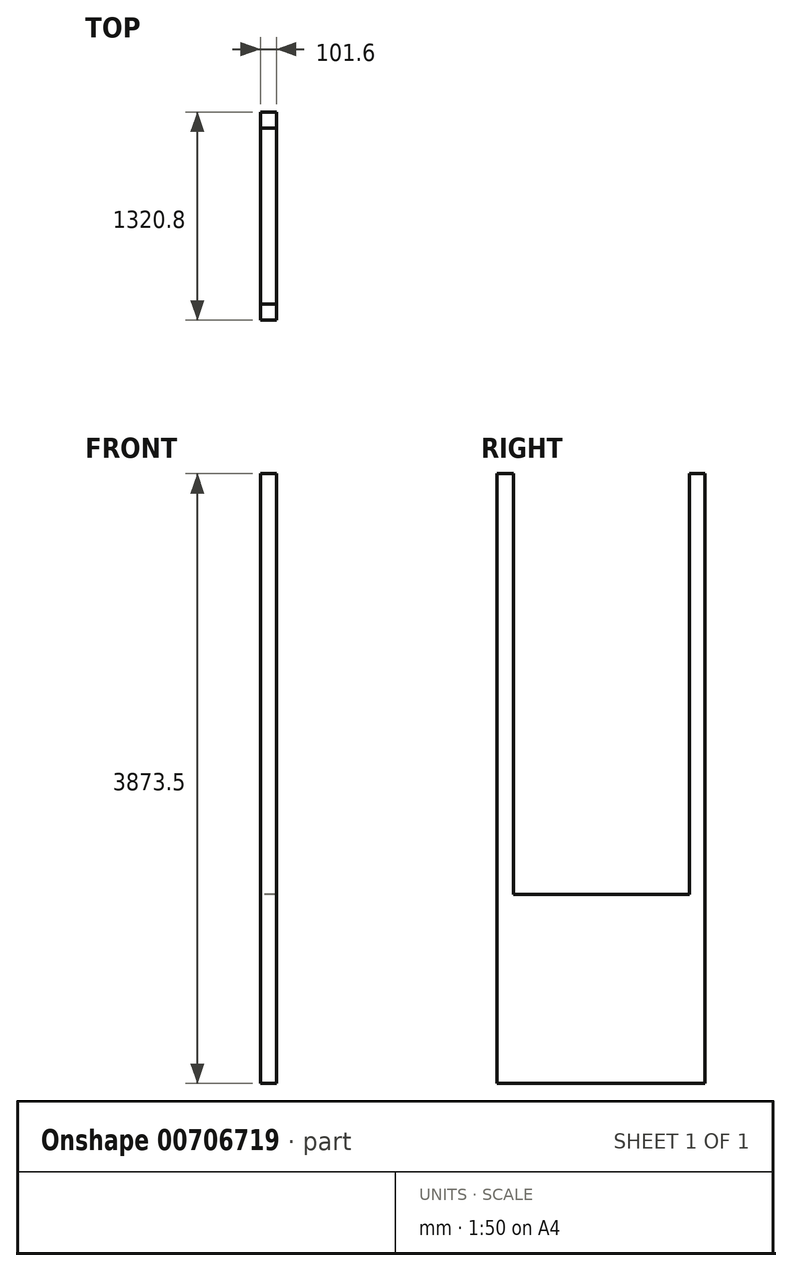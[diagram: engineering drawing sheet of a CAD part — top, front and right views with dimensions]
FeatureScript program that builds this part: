
annotation { "Feature Type Name" : "Feature", "Feature Type Description" : "" }
export const myFeature = defineFeature(function(context is Context, id is Id, definition is map)
    precondition{}
    {
        {
            var Q0;
            Q0=qCreatedBy(makeId("Right.planeOp"),FACE);
            var sketch = newSketch(context, id + "F0", { "sketchPlane" : qUnion([Q0])});
            skLineSegment(sketch, "E0.bottom", {"start": v(0, 0) * mm, "end": v(1320.8, 0) * mm});
            skLineSegment(sketch, "E0.top", {"start": v(0, 3873.5) * mm, "end": v(1320.8, 3873.5) * mm});
            skLineSegment(sketch, "E0.left", {"start": v(0, 0) * mm, "end": v(0, 3873.5) * mm});
            skLineSegment(sketch, "E0.right", {"start": v(1320.8, 0) * mm, "end": v(1320.8, 3873.5) * mm});
            skSolve(sketch);
        }
        {
            var Q0;
            Q0=makeQuery(id+"F0.imprint","IMPRINT",FACE,{"disambiguationData":[TD([[makeQuery(id+"F0.imprint","IMPRINT",EDGE,{"derivedFrom":sQuery(id+"F0.wireOp",EDGE,"E0.bottom")}),1.0]])]});
            extrude(context, id + "F1", {"entities" : qUnion([Q0]), "depth" : 101.6 * mm, "offsetDistance" : 25.4 * mm});
        }
        {
            var Q0;
            Q0=makeQuery(id+"F1.opExtrude","CAP_FACE",FACE,{"disambiguationData":[OSD([sQuery(id+"F0.wireOp",EDGE,"E0.bottom"),sQuery(id+"F0.wireOp",EDGE,"E0.top"),sQuery(id+"F0.wireOp",EDGE,"E0.left"),sQuery(id+"F0.wireOp",EDGE,"E0.right")])],"isStart":true});
            var sketch = newSketch(context, id + "F2", { "sketchPlane" : qUnion([Q0])});
            skLineSegment(sketch, "E1.bottom", {"start": v(-1219.62, 3873.5) * mm, "end": v(-102.02, 3873.5) * mm});
            skLineSegment(sketch, "E1.top", {"start": v(-1219.62, 1202.16) * mm, "end": v(-102.02, 1202.16) * mm});
            skLineSegment(sketch, "E1.left", {"start": v(-1219.62, 3873.5) * mm, "end": v(-1219.62, 1202.16) * mm});
            skLineSegment(sketch, "E1.right", {"start": v(-102.02, 3873.5) * mm, "end": v(-102.02, 1202.16) * mm});
            skSolve(sketch);
        }
        {
            var Q0;
            Q0=makeQuery(id+"F2.imprint","IMPRINT",FACE,{"disambiguationData":[TD([[makeQuery(id+"F2.imprint","IMPRINT",EDGE,{"derivedFrom":sQuery(id+"F2.wireOp",EDGE,"E1.bottom")}),1.0]])]});
            extrude(context, id + "F3", {"entities" : qUnion([Q0]), "operationType" : NewBodyOperationType.REMOVE, "oppositeDirection" : true, "depth" : 101.6 * mm, "offsetDistance" : 25.4 * mm});
        }
    });
